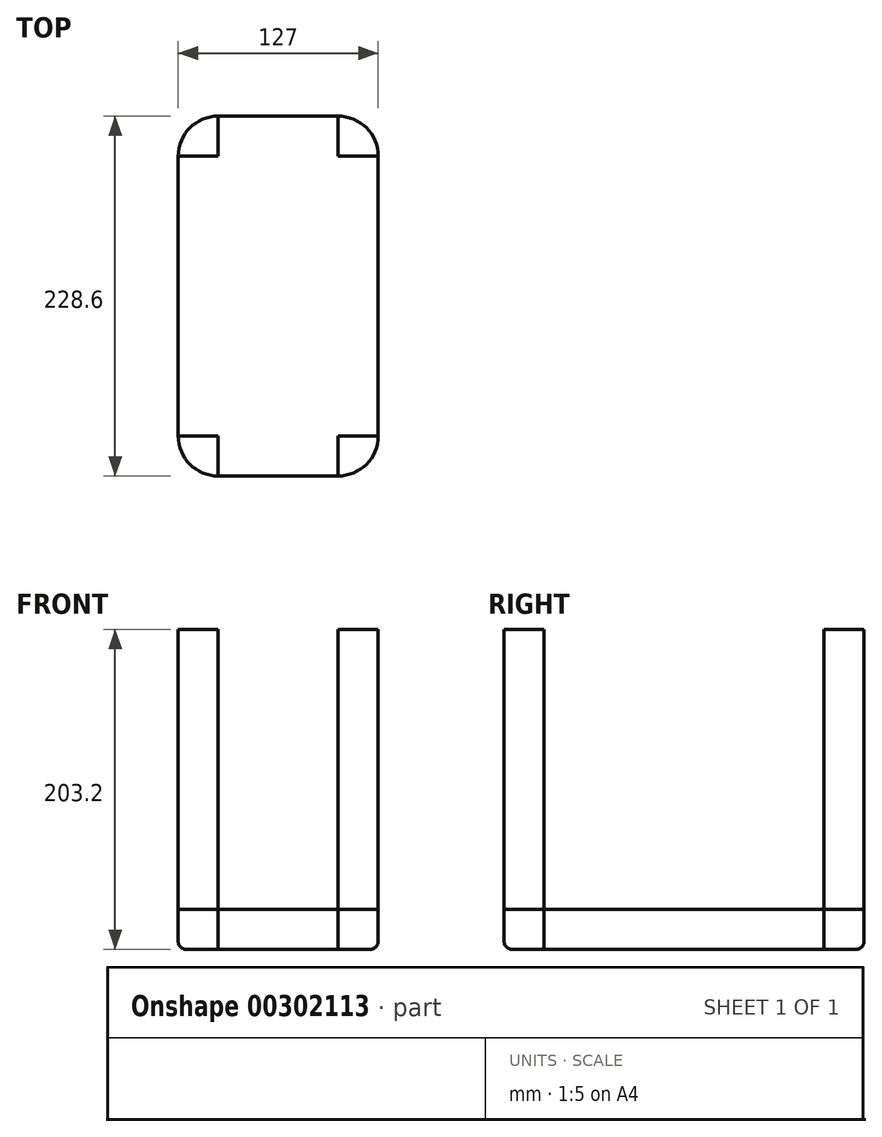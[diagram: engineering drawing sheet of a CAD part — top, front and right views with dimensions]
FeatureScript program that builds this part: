
annotation { "Feature Type Name" : "Feature", "Feature Type Description" : "" }
export const myFeature = defineFeature(function(context is Context, id is Id, definition is map)
    precondition{}
    {
        {
            var Q0;
            Q0=qCreatedBy(makeId("Front.planeOp"),FACE);
            var sketch = newSketch(context, id + "F0", { "sketchPlane" : qUnion([Q0])});
            skLineSegment(sketch, "E0.bottom", {"start": v(-100.23, 188.9) * mm, "end": v(26.77, 188.9) * mm});
            skLineSegment(sketch, "E0.top", {"start": v(-100.23, -39.7) * mm, "end": v(26.77, -39.7) * mm});
            skLineSegment(sketch, "E0.left", {"start": v(-100.23, 188.9) * mm, "end": v(-100.23, -39.7) * mm});
            skLineSegment(sketch, "E0.right", {"start": v(26.77, 188.9) * mm, "end": v(26.77, -39.7) * mm});
            skSolve(sketch);
        }
        {
            var Q0;
            Q0=makeQuery(id+"F0.imprint","IMPRINT",FACE,{"disambiguationData":[TD([[makeQuery(id+"F0.imprint","IMPRINT",EDGE,{"derivedFrom":sQuery(id+"F0.wireOp",EDGE,"E0.bottom")}),-1.0]])]});
            extrude(context, id + "F1", {"entities" : qUnion([Q0]), "depth" : 228.6 * mm});
        }
        {
            var Q0;
            Q0=makeQuery(id+"F1.opExtrude","SWEPT_FACE",FACE,{"disambiguationData":[OSD([sQuery(id+"F0.wireOp",EDGE,"E0.bottom")])]});
            shell(context, id + "F2", {"entities" : qUnion([Q0]), "thickness" : 2.54 * mm});
        }
        {
            var Q0;
            Q0=qCreatedBy(makeId("Top.planeOp"),FACE);
            var sketch = newSketch(context, id + "F3", { "sketchPlane" : qUnion([Q0])});
            skLineSegment(sketch, "E1.bottom", {"start": v(64.12, 0) * mm, "end": v(140.32, 0) * mm});
            skLineSegment(sketch, "E1.top", {"start": v(64.12, -228.6) * mm, "end": v(140.32, -228.6) * mm});
            skLineSegment(sketch, "E1.left", {"start": v(38.72, -25.4) * mm, "end": v(38.72, -203.2) * mm});
            skLineSegment(sketch, "E1.right", {"start": v(165.72, -25.4) * mm, "end": v(165.72, -203.2) * mm});
            skPoint(sketch, "E2.visualSharp", {"position": v(38.72, 0) * mm});
            skArc(sketch, "E2.filletArc", {"start": v(64.12, 0) * mm, "mid": v(46.16, -7.44) * mm, "end": v(38.72, -25.4) * mm});
            skPoint(sketch, "E3.visualSharp", {"position": v(165.72, 0) * mm});
            skArc(sketch, "E3.filletArc", {"start": v(165.72, -25.4) * mm, "mid": v(158.28, -7.44) * mm, "end": v(140.32, 0) * mm});
            skPoint(sketch, "E4.visualSharp", {"position": v(165.72, -228.6) * mm});
            skArc(sketch, "E4.filletArc", {"start": v(140.32, -228.6) * mm, "mid": v(158.28, -221.16) * mm, "end": v(165.72, -203.2) * mm});
            skPoint(sketch, "E5.visualSharp", {"position": v(38.72, -228.6) * mm});
            skArc(sketch, "E5.filletArc", {"start": v(38.72, -203.2) * mm, "mid": v(46.16, -221.16) * mm, "end": v(64.12, -228.6) * mm});
            skLineSegment(sketch, "E6", {"start": v(64.12, 0) * mm, "end": v(64.12, -25.4) * mm});
            skLineSegment(sketch, "E7", {"start": v(38.72, -25.4) * mm, "end": v(64.12, -25.4) * mm});
            skLineSegment(sketch, "E8", {"start": v(140.32, 0) * mm, "end": v(140.32, -25.4) * mm});
            skLineSegment(sketch, "E9", {"start": v(140.32, -25.4) * mm, "end": v(165.72, -25.4) * mm});
            skLineSegment(sketch, "E10", {"start": v(64.12, -203.2) * mm, "end": v(38.72, -203.2) * mm});
            skLineSegment(sketch, "E11", {"start": v(64.12, -203.2) * mm, "end": v(64.12, -228.6) * mm});
            skLineSegment(sketch, "E12", {"start": v(140.32, -228.6) * mm, "end": v(140.32, -203.2) * mm});
            skLineSegment(sketch, "E13", {"start": v(140.32, -203.2) * mm, "end": v(165.72, -203.2) * mm});
            skSolve(sketch);
        }
        {
            var Q0;
            Q0=makeQuery(id+"F3.imprint","IMPRINT",FACE,{"disambiguationData":[TD([[makeQuery(id+"F3.imprint","IMPRINT",EDGE,{"derivedFrom":sQuery(id+"F3.wireOp",EDGE,"E2.filletArc")}),1.0]])]});
            var Q1;
            Q1=makeQuery(id+"F3.imprint","IMPRINT",FACE,{"disambiguationData":[TD([[makeQuery(id+"F3.imprint","IMPRINT",EDGE,{"derivedFrom":sQuery(id+"F3.wireOp",EDGE,"E3.filletArc")}),1.0]])]});
            var Q2;
            Q2=makeQuery(id+"F3.imprint","IMPRINT",FACE,{"disambiguationData":[TD([[makeQuery(id+"F3.imprint","IMPRINT",EDGE,{"derivedFrom":sQuery(id+"F3.wireOp",EDGE,"E4.filletArc")}),1.0]])]});
            var Q3;
            Q3=makeQuery(id+"F3.imprint","IMPRINT",FACE,{"disambiguationData":[TD([[makeQuery(id+"F3.imprint","IMPRINT",EDGE,{"derivedFrom":sQuery(id+"F3.wireOp",EDGE,"E5.filletArc")}),1.0]])]});
            extrude(context, id + "F4", {"entities" : qUnion([Q0, Q1, Q2, Q3]), "depth" : 203.2 * mm});
        }
        {
            var Q0;
            Q0 = qSketchRegion(id + "F3", true);
            extrude(context, id + "F5", {"entities" : qUnion([Q0]), "depth" : 25.4 * mm});
        }
        {
            var Q0;
            Q0=makeQuery(id+"F1.opExtrude","SWEPT_BODY",BODY,{"disambiguationData":[OSD([sQuery(id+"F0.wireOp",EDGE,"E0.bottom"),sQuery(id+"F0.wireOp",EDGE,"E0.top"),sQuery(id+"F0.wireOp",EDGE,"E0.left"),sQuery(id+"F0.wireOp",EDGE,"E0.right")])]});
            deleteBodies(context, id + "F6", {"entities" : qUnion([Q0])});
        }
        {
            var Q0;
            Q0=makeQuery(id+"F5.opExtrude","CAP_FACE",FACE,{"disambiguationData":[OSD([sQuery(id+"F3.wireOp",EDGE,"E1.bottom"),sQuery(id+"F3.wireOp",EDGE,"E1.top"),sQuery(id+"F3.wireOp",EDGE,"E1.left"),sQuery(id+"F3.wireOp",EDGE,"E1.right"),sQuery(id+"F3.wireOp",EDGE,"E2.filletArc"),sQuery(id+"F3.wireOp",EDGE,"E3.filletArc"),sQuery(id+"F3.wireOp",EDGE,"E4.filletArc"),sQuery(id+"F3.wireOp",EDGE,"E5.filletArc")])],"isStart":true});
            fillet(context, id + "F7", {"entities" : qUnion([Q0]), "radius" : 5.08 * mm, "tangentPropagation" : true, "allowEdgeOverflow" : false});
        }
        {
            var Q0;
            Q0=makeQuery(id+"F4.opExtrude","CAP_EDGE",EDGE,{"disambiguationData":[OSD([sQuery(id+"F3.wireOp",EDGE,"E5.filletArc")])],"isStart":true});
            var Q1;
            Q1=makeQuery(id+"F4.opExtrude","CAP_EDGE",EDGE,{"disambiguationData":[OSD([sQuery(id+"F3.wireOp",EDGE,"E4.filletArc")])],"isStart":true});
            var Q2;
            Q2=makeQuery(id+"F4.opExtrude","CAP_EDGE",EDGE,{"disambiguationData":[OSD([sQuery(id+"F3.wireOp",EDGE,"E3.filletArc")])],"isStart":true});
            var Q3;
            Q3=makeQuery(id+"F4.opExtrude","CAP_EDGE",EDGE,{"disambiguationData":[OSD([sQuery(id+"F3.wireOp",EDGE,"E2.filletArc")])],"isStart":true});
            fillet(context, id + "F8", {"entities" : qUnion([Q0, Q1, Q2, Q3]), "radius" : 5.08 * mm, "tangentPropagation" : true, "allowEdgeOverflow" : false});
        }
    });
